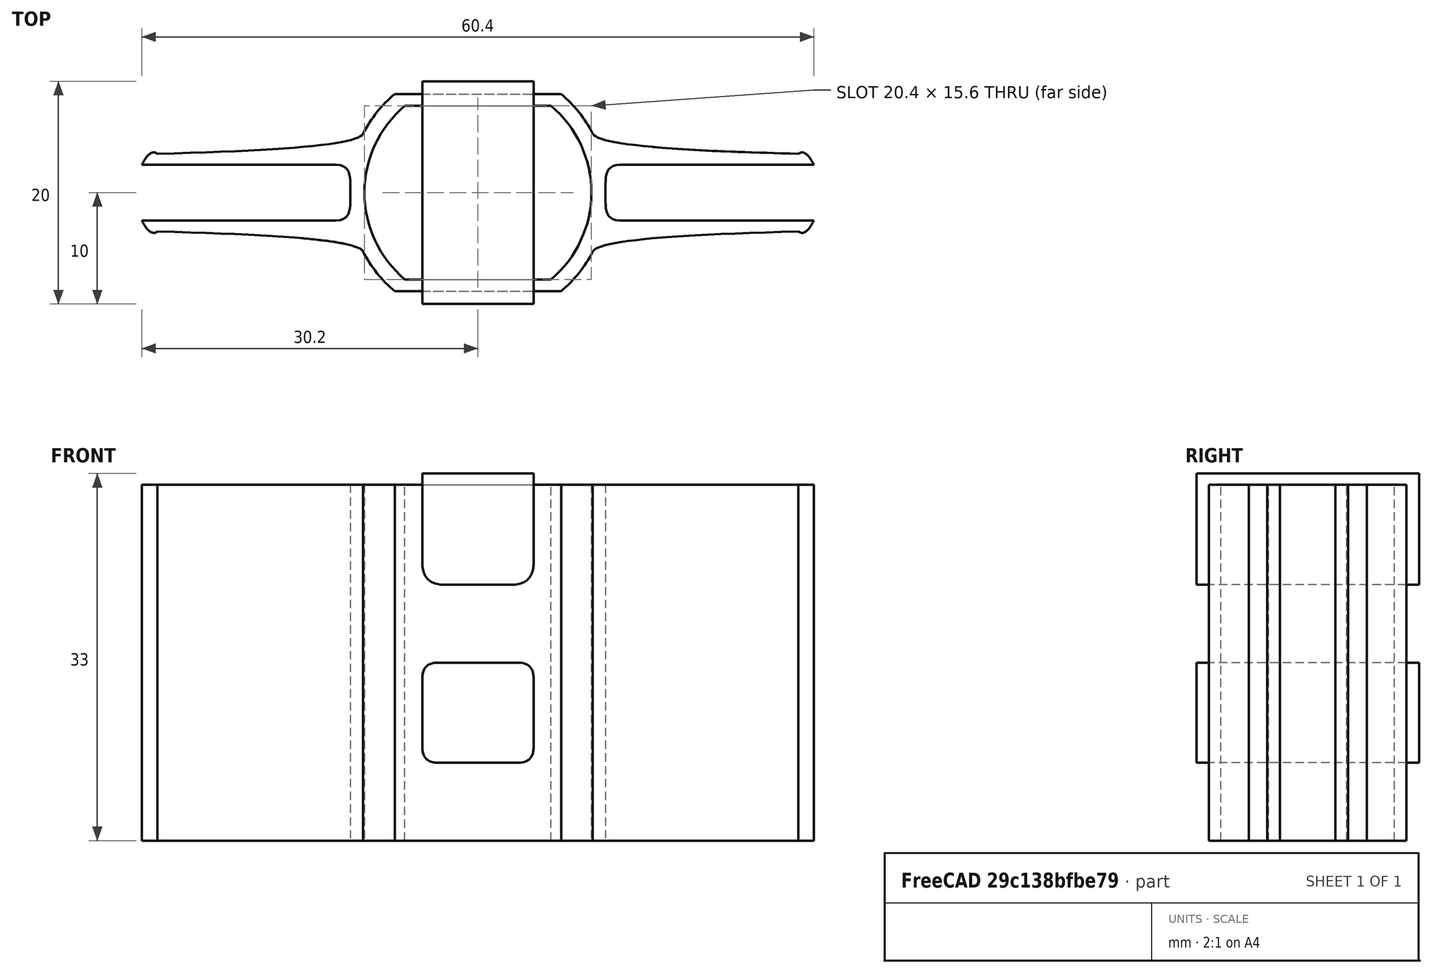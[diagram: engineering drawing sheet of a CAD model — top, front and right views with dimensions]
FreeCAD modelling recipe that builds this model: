
FCSTD DOCUMENT  (FreeCAD 0.19R0.19.2)
Label: 025
License: All rights reserved
LicenseURL: http://en.wikipedia.org/wiki/All_rights_reserved
objects: Sketcher::SketchObject×3, Part::Extrusion×2
note: 5 computed .brp shape members not serialized (recipe doc carries the construction recipe); baked Part::Feature solids carry a one-line shape summary decoded from their .brp

FEATURE [Sketcher::SketchObject] Sketch  label="main001"
  FullyConstrained = true
  sketch-geometry (80):
    g0: ArcOfCircle CenterX=-3.45031e-07 CenterY=0 CenterZ=0 NormalX=0 NormalY=0 NormalZ=1 AngleXU=0 Radius=10.2 StartAngle=5.4126 EndAngle=7.15377
    g1: ArcOfCircle CenterX=-3.45031e-07 CenterY=0 CenterZ=0 NormalX=0 NormalY=0 NormalZ=1 AngleXU=0 Radius=10.2 StartAngle=2.27101 EndAngle=4.01218
    g2: LineSegment StartX=-6.57267 StartY=7.8 StartZ=0 EndX=6.57267 EndY=7.8 EndZ=0
    g3: LineSegment StartX=-6.57267 StartY=-7.8 StartZ=0 EndX=6.57267 EndY=-7.8 EndZ=0
    g4: ArcOfCircle CenterX=-3.45031e-07 CenterY=0 CenterZ=0 NormalX=0 NormalY=0 NormalZ=1 AngleXU=0 Radius=11.6 StartAngle=2.27101 EndAngle=2.66709
    g5: ArcOfCircle CenterX=-3.45031e-07 CenterY=0 CenterZ=0 NormalX=0 NormalY=0 NormalZ=1 AngleXU=0 Radius=11.6 StartAngle=5.4126 EndAngle=5.80868
    g6: LineSegment StartX=-7.4748 StartY=8.87059 StartZ=0 EndX=7.4748 EndY=8.87059 EndZ=0
    g7: LineSegment StartX=-7.4748 StartY=-8.87059 StartZ=0 EndX=7.4748 EndY=-8.87059 EndZ=0
    g8: ArcOfCircle CenterX=-3.45031e-07 CenterY=0 CenterZ=0 NormalX=0 NormalY=0 NormalZ=1 AngleXU=0 Radius=11.6 StartAngle=3.6161 EndAngle=4.01218
    g9: ArcOfCircle CenterX=-3.45031e-07 CenterY=0 CenterZ=0 NormalX=0 NormalY=0 NormalZ=1 AngleXU=0 Radius=11.6 StartAngle=0.474503 EndAngle=0.870585
    g10: Circle CenterX=-28.8 CenterY=3.5 CenterZ=0 NormalX=0 NormalY=0 NormalZ=1 AngleXU=0 Radius=1
    g11: Circle CenterX=-10.9247 CenterY=3.9 CenterZ=0 NormalX=0 NormalY=0 NormalZ=1 AngleXU=0 Radius=1
    g12: Circle CenterX=-10.3184 CenterY=5.3 CenterZ=0 NormalX=0 NormalY=0 NormalZ=1 AngleXU=0 Radius=1
    g13: BSplineCurve PolesCount=3 KnotsCount=2 Degree=2 IsPeriodic=0
    g14: GeomPoint X=-28.8 Y=3.5 Z=0
    g15: GeomPoint X=-10.3184 Y=5.3 Z=0
    g16: Circle CenterX=28.8 CenterY=3.5 CenterZ=0 NormalX=0 NormalY=0 NormalZ=1 AngleXU=0 Radius=1
    g17: Circle CenterX=10.9247 CenterY=3.9 CenterZ=0 NormalX=0 NormalY=0 NormalZ=1 AngleXU=0 Radius=1
    g18: Circle CenterX=10.3184 CenterY=5.3 CenterZ=0 NormalX=0 NormalY=0 NormalZ=1 AngleXU=0 Radius=1
    g19: BSplineCurve PolesCount=3 KnotsCount=2 Degree=2 IsPeriodic=0
    g20: GeomPoint X=28.8 Y=3.5 Z=0
    g21: GeomPoint X=10.3184 Y=5.3 Z=0
    g22: Circle CenterX=-28.8 CenterY=-3.5 CenterZ=0 NormalX=0 NormalY=0 NormalZ=1 AngleXU=0 Radius=1
    g23: Circle CenterX=-10.9247 CenterY=-3.9 CenterZ=0 NormalX=0 NormalY=0 NormalZ=1 AngleXU=0 Radius=1
    g24: Circle CenterX=-10.3184 CenterY=-5.3 CenterZ=0 NormalX=0 NormalY=0 NormalZ=1 AngleXU=0 Radius=1
    g25: BSplineCurve PolesCount=3 KnotsCount=2 Degree=2 IsPeriodic=0
    g26: GeomPoint X=-28.8 Y=-3.5 Z=0
    g27: GeomPoint X=-10.3184 Y=-5.3 Z=0
    g28: Circle CenterX=28.8 CenterY=-3.5 CenterZ=0 NormalX=0 NormalY=0 NormalZ=1 AngleXU=0 Radius=1
    g29: Circle CenterX=10.9247 CenterY=-3.9 CenterZ=0 NormalX=0 NormalY=0 NormalZ=1 AngleXU=0 Radius=1
    g30: Circle CenterX=10.3184 CenterY=-5.3 CenterZ=0 NormalX=0 NormalY=0 NormalZ=1 AngleXU=0 Radius=1
    g31: BSplineCurve PolesCount=3 KnotsCount=2 Degree=2 IsPeriodic=0
    g32: GeomPoint X=28.8 Y=-3.5 Z=0
    g33: GeomPoint X=10.3184 Y=-5.3 Z=0
    g34-g38: Circle x5 (B-spline internal-alignment scaffolding for g39; pole/knot coordinates omitted)
    g39: BSplineCurve PolesCount=5 KnotsCount=3 Degree=3 IsPeriodic=0
    g40: GeomPoint X=12.7274 Y=2.5 Z=0
    g41: GeomPoint X=11.4637 Y=2.49999e-07 Z=0
    g42: GeomPoint X=12.7274 Y=-2.5 Z=0
    g43-g47: Circle x5 (B-spline internal-alignment scaffolding for g48; pole/knot coordinates omitted)
    g48: BSplineCurve PolesCount=5 KnotsCount=3 Degree=3 IsPeriodic=0
    g49: GeomPoint X=-12.7274 Y=2.5 Z=0
    g50: GeomPoint X=-11.4637 Y=2.50004e-07 Z=0
    g51: GeomPoint X=-12.7274 Y=-2.5 Z=0
    g52: LineSegment StartX=-30.2 StartY=-2.5 StartZ=0 EndX=-12.7274 EndY=-2.5 EndZ=0
    g53: LineSegment StartX=-30.2 StartY=2.5 StartZ=0 EndX=-12.7274 EndY=2.5 EndZ=0
    g54: LineSegment StartX=30.2 StartY=2.5 StartZ=0 EndX=12.7274 EndY=2.5 EndZ=0
    g55: LineSegment StartX=30.2 StartY=-2.5 StartZ=0 EndX=12.7274 EndY=-2.5 EndZ=0
    g56: Circle CenterX=-30.2 CenterY=2.5 CenterZ=0 NormalX=0 NormalY=0 NormalZ=1 AngleXU=0 Radius=1
    g57: Circle CenterX=-29.4304 CenterY=3.99253 CenterZ=0 NormalX=0 NormalY=0 NormalZ=1 AngleXU=0 Radius=1
    g58: Circle CenterX=-28.8 CenterY=3.5 CenterZ=0 NormalX=0 NormalY=0 NormalZ=1 AngleXU=0 Radius=1
    g59: BSplineCurve PolesCount=3 KnotsCount=2 Degree=2 IsPeriodic=0
    g60: GeomPoint X=-30.2 Y=2.5 Z=0
    g61: GeomPoint X=-28.8 Y=3.5 Z=0
    g62: Circle CenterX=30.2 CenterY=-2.5 CenterZ=0 NormalX=0 NormalY=0 NormalZ=1 AngleXU=0 Radius=1
    g63: Circle CenterX=29.4304 CenterY=-3.99253 CenterZ=0 NormalX=0 NormalY=0 NormalZ=1 AngleXU=0 Radius=1
    g64: Circle CenterX=28.8 CenterY=-3.5 CenterZ=0 NormalX=0 NormalY=0 NormalZ=1 AngleXU=0 Radius=1
    g65: BSplineCurve PolesCount=3 KnotsCount=2 Degree=2 IsPeriodic=0
    g66: GeomPoint X=30.2 Y=-2.5 Z=0
    g67: GeomPoint X=28.8 Y=-3.5 Z=0
    g68: Circle CenterX=30.2 CenterY=2.5 CenterZ=0 NormalX=0 NormalY=0 NormalZ=1 AngleXU=0 Radius=1
    g69: Circle CenterX=29.4304 CenterY=3.99253 CenterZ=0 NormalX=0 NormalY=0 NormalZ=1 AngleXU=0 Radius=1
    g70: Circle CenterX=28.8 CenterY=3.5 CenterZ=0 NormalX=0 NormalY=0 NormalZ=1 AngleXU=0 Radius=1
    g71: BSplineCurve PolesCount=3 KnotsCount=2 Degree=2 IsPeriodic=0
    g72: GeomPoint X=30.2 Y=2.5 Z=0
    g73: GeomPoint X=28.8 Y=3.5 Z=0
    g74: Circle CenterX=-30.2 CenterY=-2.5 CenterZ=0 NormalX=0 NormalY=0 NormalZ=1 AngleXU=0 Radius=1
    g75: Circle CenterX=-29.4304 CenterY=-3.99253 CenterZ=0 NormalX=0 NormalY=0 NormalZ=1 AngleXU=0 Radius=1
    g76: Circle CenterX=-28.8 CenterY=-3.5 CenterZ=0 NormalX=0 NormalY=0 NormalZ=1 AngleXU=0 Radius=1
    g77: BSplineCurve PolesCount=3 KnotsCount=2 Degree=2 IsPeriodic=0
    g78: GeomPoint X=-30.2 Y=-2.5 Z=0
    g79: GeomPoint X=-28.8 Y=-3.5 Z=0
  constraints (131):
    c: Block(g0)
    c: Equal(g0,g1)
    c: Coincident(g0,g1)
    c: Coincident(g2,g1)
    c: Coincident(g2,g0)
    c: Horizontal(g2)
    c: Coincident(g3,g1)
    c: Coincident(g3,g0)
    c: Horizontal(g3)
    c: Block(g2)
    c: Block(g3)
    c: Coincident(g4,g0)
    c: Coincident(g5,g0)
    c: Block(g5)
    c: Block(g4)
    c: Coincident(g6,g4)
    c: Coincident(g6,g9)
    c: Horizontal(g6)
    c: Coincident(g7,g8)
    c: Coincident(g7,g5)
    c: Horizontal(g7)
    c: Equal(g4,g8)
    c: Coincident(g4,g8)
    c: Equal(g5,g9)
    c: Coincident(g5,g9)
    c: Block(g8)
    c: Block(g9)
    c: Weight(g10) = 1
    c: Equal(g10,g11)
    c: Equal(g10,g12)
    c: Coincident(g13,g4)
    c: InternalAlignment(g10,g13)
    c: InternalAlignment(g11,g13)
    c: InternalAlignment(g12,g13)
    c: InternalAlignment(g14,g13)
    c: InternalAlignment(g15,g13)
    c: Weight(g16) = 1
    c: Equal(g16,g17)
    c: Equal(g16,g18)
    c: Coincident(g19,g9)
    c: InternalAlignment(g16,g19)
    c: InternalAlignment(g17,g19)
    c: InternalAlignment(g18,g19)
    c: InternalAlignment(g20,g19)
    c: InternalAlignment(g21,g19)
    c: Weight(g22) = 1
    c: Equal(g22,g23)
    c: Equal(g22,g24)
    c: Coincident(g25,g8)
    c: InternalAlignment(g22,g25)
    c: InternalAlignment(g23,g25)
    c: InternalAlignment(g24,g25)
    c: InternalAlignment(g26,g25)
    c: InternalAlignment(g27,g25)
    c: Weight(g28) = 1
    c: Equal(g28,g29)
    c: Equal(g28,g30)
    c: Coincident(g31,g5)
    c: InternalAlignment(g28,g31)
    c: InternalAlignment(g29,g31)
    c: InternalAlignment(g30,g31)
    c: InternalAlignment(g32,g31)
    c: InternalAlignment(g33,g31)
    c: Block(g19)
    c: Block(g13)
    c: Block(g31)
    c: Block(g25)
    c: Weight(g34) = 1
    c: Equal(g34, g35-g38) x4
    c: InternalAlignment(g34-g38 -> g39) x5
    c: InternalAlignment(g40,g39)
    c: InternalAlignment(g41,g39)
    c: InternalAlignment(g42,g39)
    c: Weight(g43) = 1
    c: Equal(g43,g44)
    c: Equal(g43,g45)
    c: Equal(g43,g46)
    c: InternalAlignment(g43-g47 -> g48) x5
    c: InternalAlignment(g49,g48)
    c: InternalAlignment(g50,g48)
    c: InternalAlignment(g51,g48)
    c: Block(g48)
    c: Block(g39)
    c: Coincident(g52,g48)
    c: Tangent(g52,g22)
    c: Coincident(g53,g48)
    c: Tangent(g53,g10)
    c: Coincident(g54,g39)
    c: Tangent(g54,g16)
    c: Coincident(g55,g39)
    c: Tangent(g55,g28)
    c: Weight(g56) = 1
    c: Equal(g56,g57)
    c: Equal(g56,g58)
    c: InternalAlignment(g56,g59)
    c: InternalAlignment(g57,g59)
    c: InternalAlignment(g58,g59)
    c: InternalAlignment(g60,g59)
    c: InternalAlignment(g61,g59)
    c: Weight(g62) = 1
    c: Equal(g62,g63)
    c: Equal(g62,g64)
    c: InternalAlignment(g62,g65)
    c: InternalAlignment(g63,g65)
    c: InternalAlignment(g64,g65)
    c: InternalAlignment(g66,g65)
    c: InternalAlignment(g67,g65)
    c: Weight(g68) = 1
    c: Equal(g68,g69)
    c: Equal(g68,g70)
    c: InternalAlignment(g68,g71)
    c: InternalAlignment(g69,g71)
    c: InternalAlignment(g70,g71)
    c: InternalAlignment(g72,g71)
    c: InternalAlignment(g73,g71)
    c: Block(g71)
    c: Block(g54)
    c: Block(g65)
    c: Block(g55)
    c: Weight(g74) = 1
    c: Equal(g74,g75)
    c: Equal(g74,g76)
    c: InternalAlignment(g74,g77)
    c: InternalAlignment(g75,g77)
    c: InternalAlignment(g76,g77)
    c: InternalAlignment(g78,g77)
    c: InternalAlignment(g79,g77)
    c: Block(g77)
    c: Block(g52)
    c: Block(g59)
    c: Block(g53)
FEATURE [Part::Extrusion] Extrude  label="main"
  Base = -> Sketch
  Dir = (0,0,1)
  DirMode = 2
  FaceMakerClass = Part::FaceMakerBullseye
  LengthFwd = 32
  LengthRev = 0
  Solid = true
  Symmetric = false
FEATURE [Sketcher::SketchObject] Sketch001  label="mainCollingAndStructuralHoles"
  FullyConstrained = true
  Placement = pos=(0,0,0) rot=(-1,0,0;4.71239rad)
  sketch-geometry (44):
    g0: Circle CenterX=-5 CenterY=2 CenterZ=0 NormalX=0 NormalY=0 NormalZ=1 AngleXU=0 Radius=1
    g1: Circle CenterX=-5 CenterY=0 CenterZ=0 NormalX=0 NormalY=0 NormalZ=1 AngleXU=0 Radius=1
    g2: Circle CenterX=-3 CenterY=4.6505e-12 CenterZ=0 NormalX=0 NormalY=0 NormalZ=1 AngleXU=0 Radius=1
    g3: BSplineCurve PolesCount=3 KnotsCount=2 Degree=2 IsPeriodic=0
    g4: GeomPoint X=-5 Y=2 Z=0
    g5: GeomPoint X=-3 Y=4.6505e-12 Z=0
    g6: Circle CenterX=5 CenterY=2 CenterZ=0 NormalX=0 NormalY=0 NormalZ=1 AngleXU=0 Radius=1
    g7: Circle CenterX=5 CenterY=4.6505e-12 CenterZ=0 NormalX=0 NormalY=0 NormalZ=1 AngleXU=0 Radius=1
    g8: Circle CenterX=3 CenterY=4.6505e-12 CenterZ=0 NormalX=0 NormalY=0 NormalZ=1 AngleXU=0 Radius=1
    g9: BSplineCurve PolesCount=3 KnotsCount=2 Degree=2 IsPeriodic=0
    g10: GeomPoint X=5 Y=2 Z=0
    g11: GeomPoint X=3 Y=4.6505e-12 Z=0
    g12: LineSegment StartX=5 StartY=2 StartZ=0 EndX=5 EndY=10 EndZ=0
    g13: LineSegment StartX=-5 StartY=2 StartZ=0 EndX=-5 EndY=10 EndZ=0
    g14: LineSegment StartX=-3 StartY=4.6505e-12 StartZ=0 EndX=3 EndY=4.6505e-12 EndZ=0
    g15: LineSegment StartX=-5 StartY=10 StartZ=0 EndX=5 EndY=10 EndZ=0
    g16: Circle CenterX=-3.6 CenterY=-7 CenterZ=0 NormalX=0 NormalY=0 NormalZ=1 AngleXU=0 Radius=1
    g17: Circle CenterX=-5 CenterY=-7 CenterZ=0 NormalX=0 NormalY=0 NormalZ=1 AngleXU=0 Radius=1
    g18: Circle CenterX=-5 CenterY=-8.4 CenterZ=0 NormalX=0 NormalY=0 NormalZ=1 AngleXU=0 Radius=1
    g19: BSplineCurve PolesCount=3 KnotsCount=2 Degree=2 IsPeriodic=0
    g20: GeomPoint X=-3.6 Y=-7 Z=0
    g21: GeomPoint X=-5 Y=-8.4 Z=0
    g22: Circle CenterX=5 CenterY=-8.4 CenterZ=0 NormalX=0 NormalY=0 NormalZ=1 AngleXU=0 Radius=1
    g23: Circle CenterX=5 CenterY=-7 CenterZ=0 NormalX=0 NormalY=0 NormalZ=1 AngleXU=0 Radius=1
    g24: Circle CenterX=3.6 CenterY=-7 CenterZ=0 NormalX=0 NormalY=0 NormalZ=1 AngleXU=0 Radius=1
    g25: BSplineCurve PolesCount=3 KnotsCount=2 Degree=2 IsPeriodic=0
    g26: GeomPoint X=5 Y=-8.4 Z=0
    g27: GeomPoint X=3.6 Y=-7 Z=0
    g28: Circle CenterX=-3.6 CenterY=-16 CenterZ=0 NormalX=0 NormalY=0 NormalZ=1 AngleXU=0 Radius=1
    g29: Circle CenterX=-5 CenterY=-16 CenterZ=0 NormalX=0 NormalY=0 NormalZ=1 AngleXU=0 Radius=1
    g30: Circle CenterX=-5 CenterY=-14.6 CenterZ=0 NormalX=0 NormalY=0 NormalZ=1 AngleXU=0 Radius=1
    g31: BSplineCurve PolesCount=3 KnotsCount=2 Degree=2 IsPeriodic=0
    g32: GeomPoint X=-3.6 Y=-16 Z=0
    g33: GeomPoint X=-5 Y=-14.6 Z=0
    g34: Circle CenterX=5 CenterY=-14.6 CenterZ=0 NormalX=0 NormalY=0 NormalZ=1 AngleXU=0 Radius=1
    g35: Circle CenterX=5 CenterY=-16 CenterZ=0 NormalX=0 NormalY=0 NormalZ=1 AngleXU=0 Radius=1
    g36: Circle CenterX=3.6 CenterY=-16 CenterZ=0 NormalX=0 NormalY=0 NormalZ=1 AngleXU=0 Radius=1
    g37: BSplineCurve PolesCount=3 KnotsCount=2 Degree=2 IsPeriodic=0
    g38: GeomPoint X=5 Y=-14.6 Z=0
    g39: GeomPoint X=3.6 Y=-16 Z=0
    g40: LineSegment StartX=-3.6 StartY=-7 StartZ=0 EndX=3.6 EndY=-7 EndZ=0
    g41: LineSegment StartX=-5 StartY=-8.4 StartZ=0 EndX=-5 EndY=-14.6 EndZ=0
    g42: LineSegment StartX=-3.6 StartY=-16 StartZ=0 EndX=3.6 EndY=-16 EndZ=0
    g43: LineSegment StartX=5 StartY=-14.6 StartZ=0 EndX=5 EndY=-8.4 EndZ=0
  constraints (79):
    c: Weight(g0) = 1
    c: Equal(g0,g1)
    c: Equal(g0,g2)
    c: InternalAlignment(g0,g3)
    c: InternalAlignment(g1,g3)
    c: InternalAlignment(g2,g3)
    c: InternalAlignment(g4,g3)
    c: InternalAlignment(g5,g3)
    c: Weight(g6) = 1
    c: Equal(g6,g7)
    c: Equal(g6,g8)
    c: InternalAlignment(g6,g9)
    c: InternalAlignment(g7,g9)
    c: InternalAlignment(g8,g9)
    c: InternalAlignment(g10,g9)
    c: InternalAlignment(g11,g9)
    c: Block(g3)
    c: Coincident(g13,g3)
    c: Block(g9)
    c: Coincident(g12,g9)
    c: Vertical(g12)
    c: Block(g12)
    c: Block(g13)
    c: Coincident(g14,g3)
    c: Coincident(g14,g9)
    c: Horizontal(g14)
    c: Coincident(g15,g13)
    c: Coincident(g15,g12)
    c: Horizontal(g15)
    c: Distance(g12) = 8
    c: Distance(g15) = 10
    c: Weight(g16) = 1
    c: Equal(g16,g17)
    c: Equal(g16,g18)
    c: InternalAlignment(g16,g19)
    c: InternalAlignment(g17,g19)
    c: InternalAlignment(g18,g19)
    c: InternalAlignment(g20,g19)
    c: InternalAlignment(g21,g19)
    c: Weight(g22) = 1
    c: Equal(g22,g23)
    c: Equal(g22,g24)
    c: InternalAlignment(g22,g25)
    c: InternalAlignment(g23,g25)
    c: InternalAlignment(g24,g25)
    c: InternalAlignment(g26,g25)
    c: InternalAlignment(g27,g25)
    c: Weight(g28) = 1
    c: Equal(g28,g29)
    c: Equal(g28,g30)
    c: InternalAlignment(g28,g31)
    c: InternalAlignment(g29,g31)
    c: InternalAlignment(g30,g31)
    c: InternalAlignment(g32,g31)
    c: InternalAlignment(g33,g31)
    c: Weight(g34) = 1
    c: Equal(g34,g35)
    c: Equal(g34,g36)
    c: InternalAlignment(g34,g37)
    c: InternalAlignment(g35,g37)
    c: InternalAlignment(g36,g37)
    c: InternalAlignment(g38,g37)
    c: InternalAlignment(g39,g37)
    c: Block(g25)
    c: Block(g37)
    c: Block(g31)
    c: Block(g19)
    c: Coincident(g40,g19)
    c: Coincident(g40,g25)
    c: Horizontal(g40)
    c: Coincident(g41,g19)
    c: Coincident(g41,g31)
    c: Vertical(g41)
    c: Coincident(g42,g31)
    c: Coincident(g42,g37)
    c: Horizontal(g42)
    c: Coincident(g43,g37)
    c: Coincident(g43,g25)
    c: Vertical(g43)
FEATURE [Part::Extrusion] Extrude001  label="mainCollingAndStructuralHoles001"
  Base = -> Sketch001
  Dir = (0,-1,3e-16)
  DirMode = 2
  FaceMakerClass = Part::FaceMakerBullseye
  LengthFwd = 20
  LengthRev = 0
  Placement = pos=(0,10,23) rot=(0,0,1;0rad)
  Solid = true
  Symmetric = false
FEATURE [Sketcher::SketchObject] Sketch002
  FullyConstrained = true
  Placement = pos=(0,0,0) rot=(-1,0,0;4.71239rad)
  sketch-geometry (55):
    g0: LineSegment StartX=-28.43 StartY=13.1 StartZ=0 EndX=-28.43 EndY=4.4 EndZ=0
    g1: LineSegment StartX=-28.43 StartY=27.6 StartZ=0 EndX=-28.43 EndY=18.9 EndZ=0
    g2: LineSegment StartX=-12.73 StartY=25.6 StartZ=0 EndX=-12.73 EndY=19.9 EndZ=0
    g3: LineSegment StartX=-12.73 StartY=12.1 StartZ=0 EndX=-12.73 EndY=6.4 EndZ=0
    g4: Circle CenterX=-28.43 CenterY=27.6 CenterZ=0 NormalX=0 NormalY=0 NormalZ=1 AngleXU=0 Radius=1
    g5: Circle CenterX=-28.43 CenterY=29 CenterZ=0 NormalX=0 NormalY=0 NormalZ=1 AngleXU=0 Radius=1
    g6: Circle CenterX=-27.03 CenterY=29 CenterZ=0 NormalX=0 NormalY=0 NormalZ=1 AngleXU=0 Radius=1
    g7: BSplineCurve PolesCount=3 KnotsCount=2 Degree=2 IsPeriodic=0
    g8: GeomPoint X=-28.43 Y=27.6 Z=0
    g9: GeomPoint X=-27.03 Y=29 Z=0
    g10: Circle CenterX=-14.13 CenterY=27 CenterZ=0 NormalX=0 NormalY=0 NormalZ=1 AngleXU=0 Radius=1
    g11: Circle CenterX=-12.73 CenterY=27 CenterZ=0 NormalX=0 NormalY=0 NormalZ=1 AngleXU=0 Radius=1
    g12: Circle CenterX=-12.73 CenterY=25.6 CenterZ=0 NormalX=0 NormalY=0 NormalZ=1 AngleXU=0 Radius=1
    g13: BSplineCurve PolesCount=3 KnotsCount=2 Degree=2 IsPeriodic=0
    g14: GeomPoint X=-14.13 Y=27 Z=0
    g15: GeomPoint X=-12.73 Y=25.6 Z=0
    g16: Circle CenterX=-14.13 CenterY=18.5 CenterZ=0 NormalX=0 NormalY=0 NormalZ=1 AngleXU=0 Radius=1
    g17: Circle CenterX=-12.73 CenterY=18.5 CenterZ=0 NormalX=0 NormalY=0 NormalZ=1 AngleXU=0 Radius=1
    g18: Circle CenterX=-12.73 CenterY=19.9 CenterZ=0 NormalX=0 NormalY=0 NormalZ=1 AngleXU=0 Radius=1
    g19: BSplineCurve PolesCount=3 KnotsCount=2 Degree=2 IsPeriodic=0
    g20: GeomPoint X=-14.13 Y=18.5 Z=0
    g21: GeomPoint X=-12.73 Y=19.9 Z=0
    g22: Circle CenterX=-27.03 CenterY=17.5 CenterZ=0 NormalX=0 NormalY=0 NormalZ=1 AngleXU=0 Radius=1
    g23: Circle CenterX=-28.43 CenterY=17.5 CenterZ=0 NormalX=0 NormalY=0 NormalZ=1 AngleXU=0 Radius=1
    g24: Circle CenterX=-28.43 CenterY=18.9 CenterZ=0 NormalX=0 NormalY=0 NormalZ=1 AngleXU=0 Radius=1
    g25: BSplineCurve PolesCount=3 KnotsCount=2 Degree=2 IsPeriodic=0
    g26: GeomPoint X=-27.03 Y=17.5 Z=0
    g27: GeomPoint X=-28.43 Y=18.9 Z=0
    g28: Circle CenterX=-27.03 CenterY=14.5 CenterZ=0 NormalX=0 NormalY=0 NormalZ=1 AngleXU=0 Radius=1
    g29: Circle CenterX=-28.43 CenterY=14.5 CenterZ=0 NormalX=0 NormalY=0 NormalZ=1 AngleXU=0 Radius=1
    g30: Circle CenterX=-28.43 CenterY=13.1 CenterZ=0 NormalX=0 NormalY=0 NormalZ=1 AngleXU=0 Radius=1
    g31: BSplineCurve PolesCount=3 KnotsCount=2 Degree=2 IsPeriodic=0
    g32: GeomPoint X=-27.03 Y=14.5 Z=0
    g33: GeomPoint X=-28.43 Y=13.1 Z=0
    g34: Circle CenterX=-14.13 CenterY=13.5 CenterZ=0 NormalX=0 NormalY=0 NormalZ=1 AngleXU=0 Radius=1
    g35: Circle CenterX=-12.73 CenterY=13.5 CenterZ=0 NormalX=0 NormalY=0 NormalZ=1 AngleXU=0 Radius=1
    g36: Circle CenterX=-12.73 CenterY=12.1 CenterZ=0 NormalX=0 NormalY=0 NormalZ=1 AngleXU=0 Radius=1
    g37: BSplineCurve PolesCount=3 KnotsCount=2 Degree=2 IsPeriodic=0
    g38: GeomPoint X=-14.13 Y=13.5 Z=0
    g39: GeomPoint X=-12.73 Y=12.1 Z=0
    g40: Circle CenterX=-27.03 CenterY=3 CenterZ=0 NormalX=0 NormalY=0 NormalZ=1 AngleXU=0 Radius=1
    g41: Circle CenterX=-28.43 CenterY=3 CenterZ=0 NormalX=0 NormalY=0 NormalZ=1 AngleXU=0 Radius=1
    g42: Circle CenterX=-28.43 CenterY=4.4 CenterZ=0 NormalX=0 NormalY=0 NormalZ=1 AngleXU=0 Radius=1
    g43: BSplineCurve PolesCount=3 KnotsCount=2 Degree=2 IsPeriodic=0
    g44: GeomPoint X=-28.43 Y=4.4 Z=0
    g45: Circle CenterX=-14.13 CenterY=5 CenterZ=0 NormalX=0 NormalY=0 NormalZ=1 AngleXU=0 Radius=1
    g46: Circle CenterX=-12.73 CenterY=5 CenterZ=0 NormalX=0 NormalY=0 NormalZ=1 AngleXU=0 Radius=1
    g47: Circle CenterX=-12.73 CenterY=6.4 CenterZ=0 NormalX=0 NormalY=0 NormalZ=1 AngleXU=0 Radius=1
    g48: BSplineCurve PolesCount=3 KnotsCount=2 Degree=2 IsPeriodic=0
    g49: GeomPoint X=-14.13 Y=5 Z=0
    g50: GeomPoint X=-12.73 Y=6.4 Z=0
    g51: LineSegment StartX=-27.03 StartY=3 StartZ=0 EndX=-14.13 EndY=5 EndZ=0
    g52: LineSegment StartX=-27.03 StartY=14.5 StartZ=0 EndX=-14.13 EndY=13.5 EndZ=0
    g53: LineSegment StartX=-27.03 StartY=17.5 StartZ=0 EndX=-14.13 EndY=18.5 EndZ=0
    g54: LineSegment StartX=-27.03 StartY=29 StartZ=0 EndX=-14.13 EndY=27 EndZ=0
  constraints (91):
    c: Distance(g0) = 8.7
    c: Vertical(g0)
    c: Equal(g0,g1) = 8.7
    c: Vertical(g1)
    c: Vertical(g2)
    c: Distance(g2) = 5.7
    c: Vertical(g3)
    c: Equal(g2,g3) = 7.1
    c: Weight(g4) = 1
    c: Equal(g4,g5)
    c: Equal(g4,g6)
    c: InternalAlignment(g4,g7)
    c: InternalAlignment(g5,g7)
    c: InternalAlignment(g6,g7)
    c: InternalAlignment(g8,g7)
    c: InternalAlignment(g9,g7)
    c: Weight(g10) = 1
    c: Equal(g10,g11)
    c: Equal(g10,g12)
    c: InternalAlignment(g10,g13)
    c: InternalAlignment(g11,g13)
    c: InternalAlignment(g12,g13)
    c: InternalAlignment(g14,g13)
    c: InternalAlignment(g15,g13)
    c: Weight(g16) = 1
    c: Equal(g16,g17)
    c: Equal(g16,g18)
    c: Coincident(g19,g2)
    c: InternalAlignment(g16,g19)
    c: InternalAlignment(g17,g19)
    c: InternalAlignment(g18,g19)
    c: InternalAlignment(g20,g19)
    c: InternalAlignment(g21,g19)
    c: Weight(g22) = 1
    c: Equal(g22,g23)
    c: Equal(g22,g24)
    c: Coincident(g25,g1)
    c: InternalAlignment(g22,g25)
    c: InternalAlignment(g23,g25)
    c: InternalAlignment(g24,g25)
    c: InternalAlignment(g26,g25)
    c: InternalAlignment(g27,g25)
    c: Weight(g28) = 1
    c: Equal(g28,g29)
    c: Equal(g28,g30)
    c: Coincident(g31,g0)
    c: InternalAlignment(g28,g31)
    c: InternalAlignment(g29,g31)
    c: InternalAlignment(g30,g31)
    c: InternalAlignment(g32,g31)
    c: InternalAlignment(g33,g31)
    c: Weight(g34) = 1
    c: Equal(g34,g35)
    c: Equal(g34,g36)
    c: Coincident(g37,g3)
    c: InternalAlignment(g34,g37)
    c: InternalAlignment(g35,g37)
    c: InternalAlignment(g36,g37)
    c: InternalAlignment(g38,g37)
    c: InternalAlignment(g39,g37)
    c: Weight(g40) = 1
    c: Equal(g40,g41)
    c: Equal(g40,g42)
    c: InternalAlignment(g40,g43)
    c: InternalAlignment(g41,g43)
    c: InternalAlignment(g42,g43)
    c: InternalAlignment(g44,g43)
    c: Weight(g45) = 1
    c: Equal(g45,g46)
    c: Equal(g45,g47)
    c: InternalAlignment(g45,g48)
    c: InternalAlignment(g46,g48)
    c: InternalAlignment(g47,g48)
    c: InternalAlignment(g49,g48)
    c: InternalAlignment(g50,g48)
    c: Block(g54)
    c: Block(g53)
    c: Block(g52)
    c: Block(g51)
    c: Block(g43)
    c: Block(g2)
    c: Block(g19)
    c: Block(g13)
    c: Block(g7)
    c: Block(g1)
    c: Block(g25)
    c: Block(g3)
    c: Block(g37)
    c: Block(g48)
    c: Block(g0)
    c: Block(g31)
